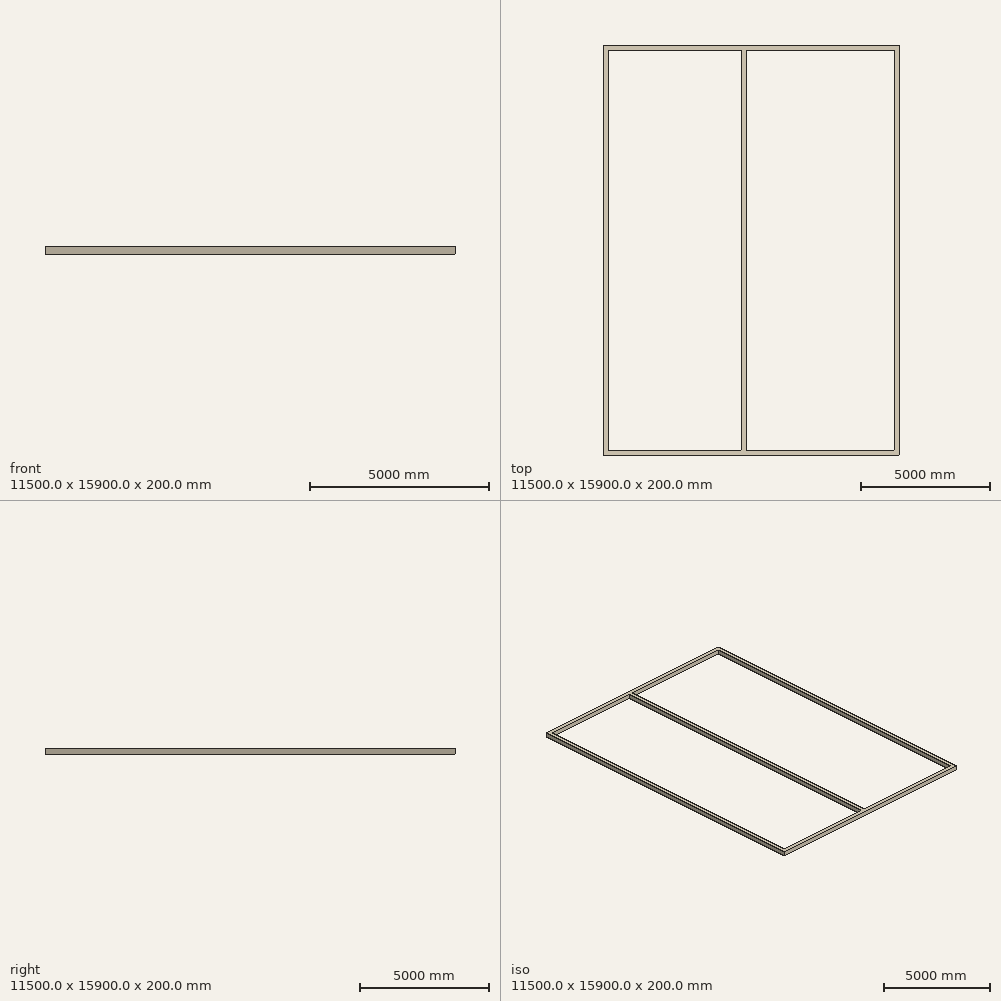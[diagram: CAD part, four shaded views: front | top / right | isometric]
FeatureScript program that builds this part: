
annotation { "Feature Type Name" : "Feature", "Feature Type Description" : "" }
export const myFeature = defineFeature(function(context is Context, id is Id, definition is map)
    precondition{}
    {
        {
            var Q0;
            Q0=qCreatedBy(makeId("Top.planeOp"),FACE);
            var sketch = newSketch(context, id + "F0", { "sketchPlane" : qUnion([Q0])});
            skLineSegment(sketch, "E0.bottom", {"start": v(5550, 7750) * mm, "end": v(-5550, 7750) * mm, "construction": true});
            skLineSegment(sketch, "E0.top", {"start": v(5550, -7750) * mm, "end": v(-5550, -7750) * mm, "construction": true});
            skLineSegment(sketch, "E0.left", {"start": v(5550, 7750) * mm, "end": v(5550, -7750) * mm, "construction": true});
            skLineSegment(sketch, "E0.right", {"start": v(-5550, 7750) * mm, "end": v(-5550, -7750) * mm, "construction": true});
            skPoint(sketch, "E0.middle", {"position": v(0, 0) * mm});
            skLineSegment(sketch, "E1", {"start": v(-300, -7750) * mm, "end": v(-300, 7750) * mm, "construction": true});
            skPoint(sketch, "E2", {"position": v(-5550, 0) * mm});
            skPoint(sketch, "E3", {"position": v(-5550, 3800) * mm});
            skPoint(sketch, "E4", {"position": v(-5550, -3800) * mm});
            skPoint(sketch, "E5", {"position": v(5550, -3800) * mm});
            skPoint(sketch, "E6", {"position": v(5550, 0) * mm});
            skPoint(sketch, "E7", {"position": v(5550, 3800) * mm});
            skLineSegment(sketch, "E8", {"start": v(900, 7750) * mm, "end": v(900, -7750) * mm, "construction": true});
            skLineSegment(sketch, "E9", {"start": v(5550, 3800) * mm, "end": v(900, 3800) * mm, "construction": true});
            skLineSegment(sketch, "E10", {"start": v(5550, 0) * mm, "end": v(900, 0) * mm, "construction": true});
            skLineSegment(sketch, "E11", {"start": v(5550, -3800) * mm, "end": v(900, -3800) * mm, "construction": true});
            skLineSegment(sketch, "E12", {"start": v(5550, 4900) * mm, "end": v(2550, 4900) * mm, "construction": true});
            skLineSegment(sketch, "E13", {"start": v(2550, 4900) * mm, "end": v(2550, 2700) * mm, "construction": true});
            skLineSegment(sketch, "E14", {"start": v(2550, -4900) * mm, "end": v(5550, -4900) * mm, "construction": true});
            skLineSegment(sketch, "E15", {"start": v(-4350, 7750) * mm, "end": v(-4350, 1750) * mm, "construction": true});
            skLineSegment(sketch, "E16", {"start": v(-4350, 1750) * mm, "end": v(-300, 1750) * mm, "construction": true});
            skLineSegment(sketch, "E17", {"start": v(-4350, 4750) * mm, "end": v(-3250, 4750) * mm, "construction": true});
            skLineSegment(sketch, "E18", {"start": v(-3250, 4750) * mm, "end": v(-3250, 7750) * mm, "construction": true});
            skLineSegment(sketch, "E19", {"start": v(-5550, 0) * mm, "end": v(-2550, 0) * mm, "construction": true});
            skLineSegment(sketch, "E20", {"start": v(-2550, 0) * mm, "end": v(-2550, -3800) * mm, "construction": true});
            skLineSegment(sketch, "E21", {"start": v(-2550, -3800) * mm, "end": v(-5550, -3800) * mm, "construction": true});
            skLineSegment(sketch, "E22", {"start": v(-5550, -2700) * mm, "end": v(-2550, -2700) * mm, "construction": true});
            skLineSegment(sketch, "E23", {"start": v(2550, 2700) * mm, "end": v(5550, 2700) * mm, "construction": true});
            skLineSegment(sketch, "E24", {"start": v(2550, -2700) * mm, "end": v(5550, -2700) * mm, "construction": true});
            skLineSegment(sketch, "E25.trimOffspring", {"start": v(2550, -2700) * mm, "end": v(2550, -4900) * mm, "construction": true});
            skPoint(sketch, "E26", {"position": v(-300, 0) * mm});
            skPoint(sketch, "E27", {"position": v(-300, 3800) * mm});
            skPoint(sketch, "E28", {"position": v(-300, -3800) * mm});
            skSolve(sketch);
        }
        {
            var Q0;
            Q0=qCreatedBy(makeId("Top.planeOp"),FACE);
            var sketch = newSketch(context, id + "F1", { "sketchPlane" : qUnion([Q0])});
            skLineSegment(sketch, "E29.0", {"start": v(5750, 7950) * mm, "end": v(-5750, 7950) * mm});
            skLineSegment(sketch, "E29.1", {"start": v(5750, 7950) * mm, "end": v(5750, -7950) * mm});
            skLineSegment(sketch, "E29.2", {"start": v(5750, -7950) * mm, "end": v(-5750, -7950) * mm});
            skLineSegment(sketch, "E29.3", {"start": v(-5750, 7950) * mm, "end": v(-5750, -7950) * mm});
            skLineSegment(sketch, "E30", {"start": v(-5750, -7950) * mm, "end": v(-5550, -7750) * mm, "construction": true});
            skPoint(sketch, "E31", {"position": v(-5650, -7850) * mm});
            skLineSegment(sketch, "E32.0", {"start": v(-5550, 7750) * mm, "end": v(-5550, -7750) * mm});
            skLineSegment(sketch, "E33.0", {"start": v(5550, 7750) * mm, "end": v(5550, -7750) * mm});
            skPoint(sketch, "E34.0", {"position": v(-300, 0) * mm});
            skLineSegment(sketch, "E35.bottom", {"start": v(-400, 7750) * mm, "end": v(-200, 7750) * mm, "construction": true});
            skLineSegment(sketch, "E35.top", {"start": v(-400, -7750) * mm, "end": v(-200, -7750) * mm, "construction": true});
            skLineSegment(sketch, "E35.left", {"start": v(-400, 7750) * mm, "end": v(-400, -7750) * mm});
            skLineSegment(sketch, "E35.right", {"start": v(-200, 7750) * mm, "end": v(-200, -7750) * mm});
            skLineSegment(sketch, "E36", {"start": v(-5550, -7750) * mm, "end": v(-400, -7750) * mm});
            skLineSegment(sketch, "E37", {"start": v(-200, -7750) * mm, "end": v(5550, -7750) * mm});
            skLineSegment(sketch, "E38", {"start": v(5550, 7750) * mm, "end": v(-200, 7750) * mm});
            skLineSegment(sketch, "E39", {"start": v(-5550, 7750) * mm, "end": v(-400, 7750) * mm});
            skSolve(sketch);
        }
        {
            var Q0;
            Q0 = qSketchRegion(id + "F1", true);
            extrude(context, id + "F2", {"entities" : qUnion([Q0]), "depth" : 200 * mm});
        }
    });
